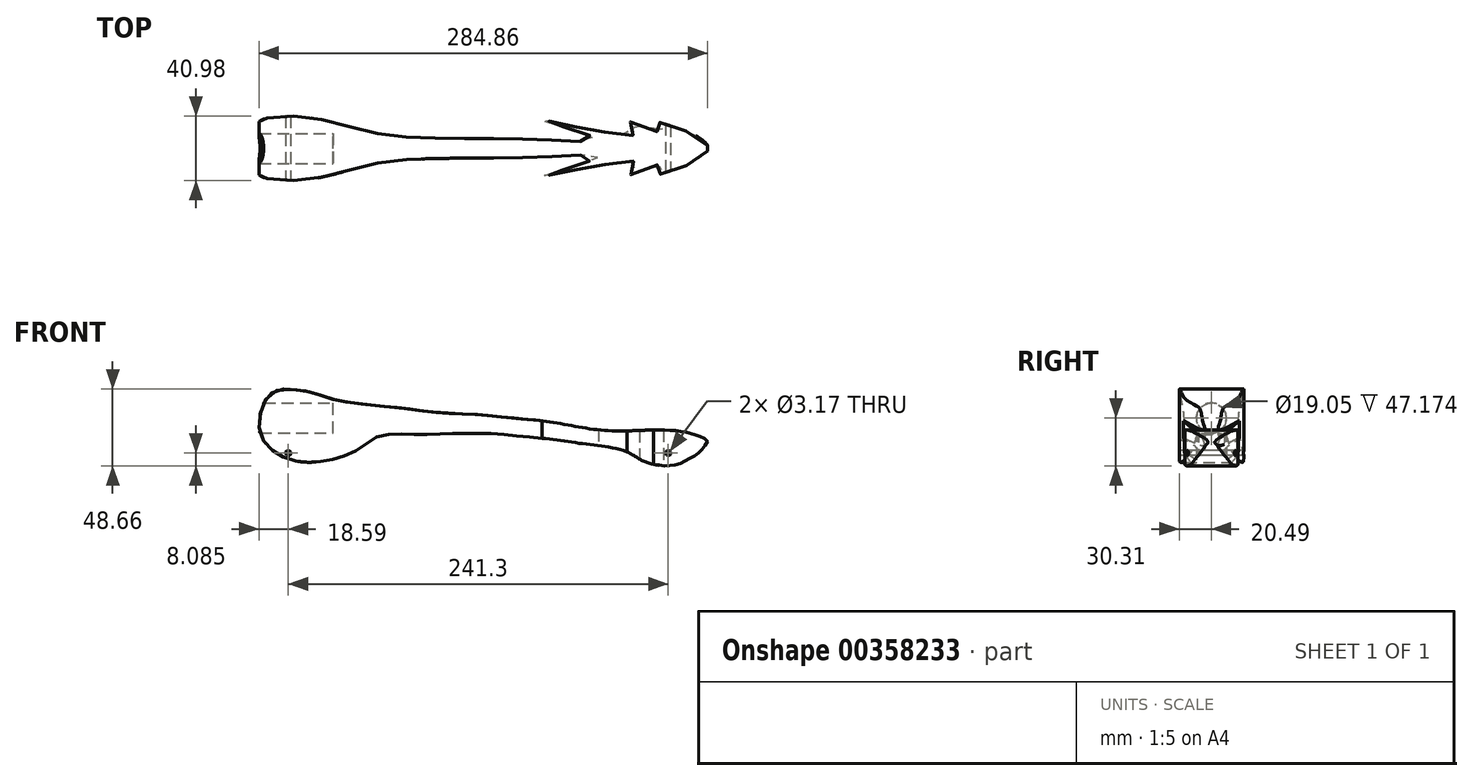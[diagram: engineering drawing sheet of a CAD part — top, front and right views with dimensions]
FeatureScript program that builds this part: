
annotation { "Feature Type Name" : "Feature", "Feature Type Description" : "" }
export const myFeature = defineFeature(function(context is Context, id is Id, definition is map)
    precondition{}
    {
        {
            var Q0;
            Q0=qCreatedBy(makeId("Front.planeOp"),FACE);
            var sketch = newSketch(context, id + "F0", { "sketchPlane" : qUnion([Q0])});
            skLineSegment(sketch, "E0.bottom", {"start": v(-146.05, 31.75) * mm, "end": v(146.05, 31.75) * mm, "construction": true});
            skLineSegment(sketch, "E0.top", {"start": v(-146.05, -31.75) * mm, "end": v(146.05, -31.75) * mm, "construction": true});
            skLineSegment(sketch, "E0.right", {"start": v(146.05, 31.75) * mm, "end": v(146.05, -31.75) * mm, "construction": true});
            skFitSpline(sketch, "E1", {"points": [v(-136.2, -14.62) * mm, v(-138.85, 0.53) * mm, v(-131.48, 15.9) * mm, v(-117.5, 18.07) * mm, v(-102.75, 15.46) * mm, v(-94.61, 12.53) * mm, v(-65.85, 8) * mm, v(-48.1, 6.27) * mm, v(-27.57, 3.63) * mm, v(-2.49, 2.35) * mm, v(22.66, 0) * mm, v(46.66, -2.62) * mm, v(70.9, -6.8) * mm, v(94.36, -8.14) * mm, v(129.95, -8.6) * mm, v(145.3, -14.19) * mm, v(145.3, -15.82) * mm, v(139.48, -22.56) * mm, v(135.76, -24.89) * mm, v(126.23, -29.54) * mm, v(112.27, -29.54) * mm, v(103.27, -26.45) * mm, v(92.86, -20.86) * mm, v(67.1, -16.38) * mm, v(47.85, -13.7) * mm, v(23.9, -11.23) * mm, v(1.46, -9.66) * mm, v(-39.43, -10.36) * mm, v(-63.52, -11.57) * mm, v(-76.47, -20.03) * mm, v(-112.93, -27.71) * mm, v(-136.2, -14.62) * mm]});
            skLineSegment(sketch, "E2.bottom", {"start": v(-146.05, 9.52) * mm, "end": v(-95.25, 9.52) * mm, "construction": true});
            skLineSegment(sketch, "E2.top", {"start": v(-141.83, -9.52) * mm, "end": v(-95.25, -9.52) * mm, "construction": true});
            skLineSegment(sketch, "E2.right", {"start": v(-95.25, 9.52) * mm, "end": v(-95.25, -9.52) * mm, "construction": true});
            skLineSegment(sketch, "E3", {"start": v(-146.05, 31.75) * mm, "end": v(-146.05, -31.75) * mm, "construction": true});
            skSolve(sketch);
        }
        {
            var Q0;
            Q0=qCreatedBy(makeId("Top.planeOp"),FACE);
            var sketch = newSketch(context, id + "F1", { "sketchPlane" : qUnion([Q0])});
            skLineSegment(sketch, "E4.bottom", {"start": v(-146.05, 22.22) * mm, "end": v(146.05, 22.23) * mm, "construction": true});
            skLineSegment(sketch, "E4.top", {"start": v(-146.05, -22.23) * mm, "end": v(146.05, -22.22) * mm, "construction": true});
            skLineSegment(sketch, "E4.left", {"start": v(-146.05, 22.22) * mm, "end": v(-146.05, -22.23) * mm, "construction": true});
            skLineSegment(sketch, "E4.right", {"start": v(146.05, 22.22) * mm, "end": v(146.05, -22.22) * mm, "construction": true});
            skLineSegment(sketch, "E5", {"start": v(-146.05, 0) * mm, "end": v(146.05, 0) * mm, "construction": true});
            skFitSpline(sketch, "E6", {"points": [v(-146.05, 0) * mm, v(-142.2, 13.58) * mm, v(-135.88, 18.7) * mm, v(-104.13, 19.17) * mm, v(-62.87, 9.3) * mm, v(-1.46, 6.28) * mm, v(55.75, 4.88) * mm, v(75.99, 5.81) * mm, v(40.63, 17.9) * mm, v(102.38, 9.16) * mm, v(94.6, 17.21) * mm, v(117.7, 9.64) * mm, v(111.45, 16.26) * mm, v(146.05, 0) * mm], "startDerivative": vector(0, 335.54) * mm, "endDerivative": vector(0, -277.49) * mm});
            skFitSpline(sketch, "E7.MirrorCS", {"points": [v(-146.05, 0) * mm, v(-142.2, -13.58) * mm, v(-135.88, -18.7) * mm, v(-104.13, -19.17) * mm, v(-62.87, -9.3) * mm, v(-1.46, -6.28) * mm, v(55.75, -4.88) * mm, v(75.99, -5.81) * mm, v(40.63, -17.9) * mm, v(102.38, -9.16) * mm, v(94.6, -17.21) * mm, v(117.7, -9.64) * mm, v(111.45, -16.26) * mm, v(146.05, 0) * mm], "startDerivative": vector(0, -335.54) * mm, "endDerivative": vector(0, 277.49) * mm});
            skLineSegment(sketch, "E8.MirrorCS", {"start": v(-146.05, -22.23) * mm, "end": v(146.05, -22.23) * mm});
            skSolve(sketch);
        }
        {
            var Q0;
            Q0=qCreatedBy(makeId("Right.planeOp"),FACE);
            var sketch = newSketch(context, id + "F2", { "sketchPlane" : qUnion([Q0])});
            skCircle(sketch, "E9", {"center": v(0, 0) * mm, "radius": 9.53 * mm});
            skSolve(sketch);
        }
        {
            var Q0;
            Q0=qCreatedBy(makeId("Front.planeOp"),FACE);
            var sketch = newSketch(context, id + "F3", { "sketchPlane" : qUnion([Q0])});
            skCircle(sketch, "E10", {"center": v(-120.65, -22.22) * mm, "radius": 1.59 * mm});
            skCircle(sketch, "E11", {"center": v(120.65, -22.23) * mm, "radius": 1.59 * mm});
            skSolve(sketch);
        }
        {
            var Q0;
            Q0=qSketchRegion(id+"F0",true);
            extrude(context, id + "F4", {"entities" : qUnion([Q0]), "depth" : 44.45 * mm, "symmetric" : true});
        }
        {
            var Q0;
            Q0=qSketchRegion(id+"F1",true);
            extrude(context, id + "F5", {"entities" : qUnion([Q0]), "operationType" : NewBodyOperationType.INTERSECT, "endBound" : BoundingType.THROUGH_ALL, "oppositeDirection" : true, "depth" : 60.96 * mm, "hasSecondDirection" : true, "secondDirectionBound" : BoundingType.THROUGH_ALL, "secondDirectionOppositeDirection" : false, "secondDirectionDepth" : 25.4 * mm});
        }
        {
            var Q0;
            Q0=qSketchRegion(id+"F2",true);
            extrude(context, id + "F6", {"entities" : qUnion([Q0]), "operationType" : NewBodyOperationType.REMOVE, "oppositeDirection" : true, "depth" : 152.4 * mm, "hasSecondDirection" : true, "secondDirectionOppositeDirection" : true, "secondDirectionDepth" : 92.07 * mm});
        }
        {
            var Q0;
            Q0=qSketchRegion(id+"F3",true);
            extrude(context, id + "F7", {"entities" : qUnion([Q0]), "operationType" : NewBodyOperationType.REMOVE, "oppositeDirection" : true, "depth" : 50.8 * mm, "symmetric" : true});
        }
    });
